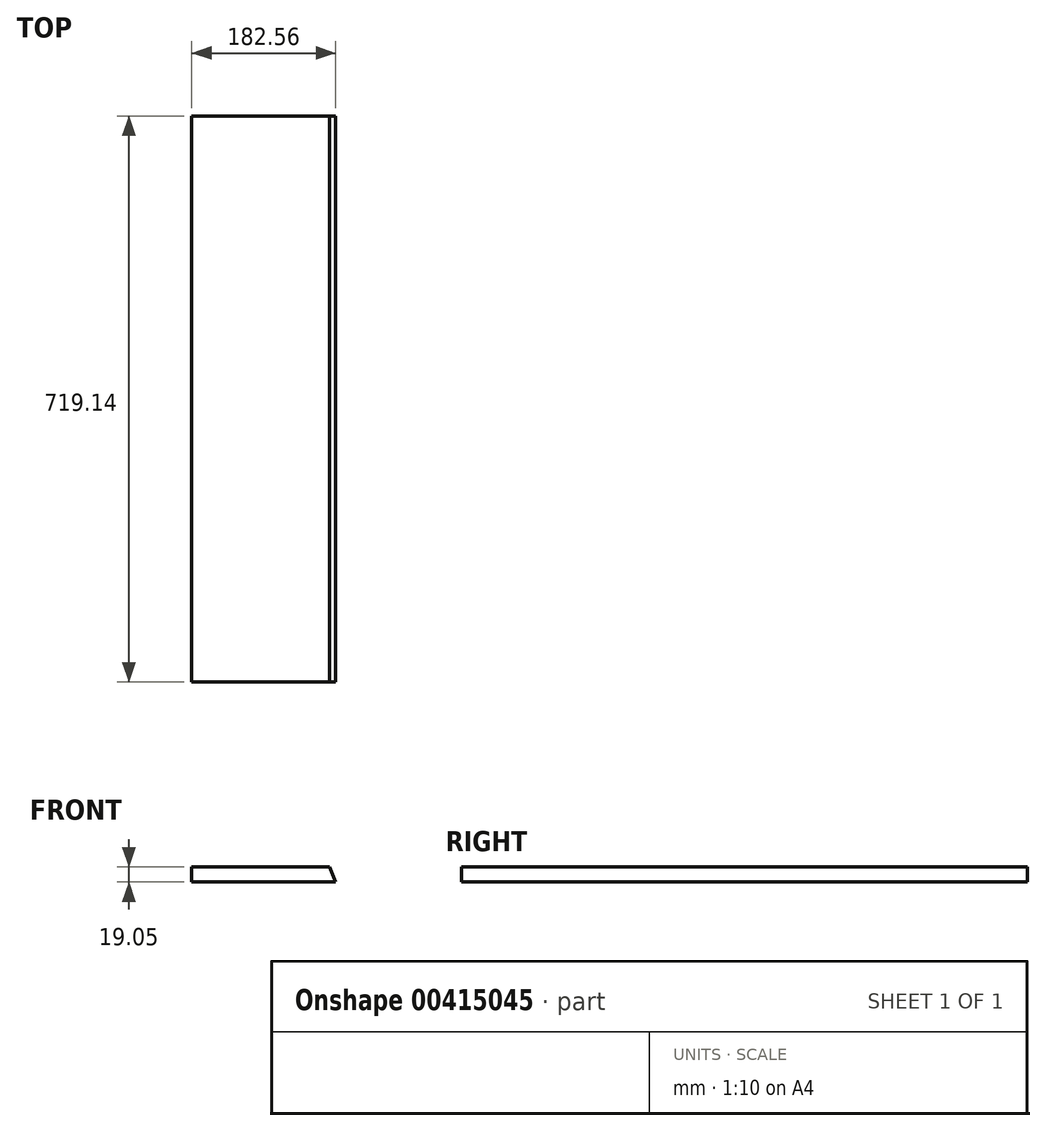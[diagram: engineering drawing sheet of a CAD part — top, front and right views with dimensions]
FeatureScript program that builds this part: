
annotation { "Feature Type Name" : "Feature", "Feature Type Description" : "" }
export const myFeature = defineFeature(function(context is Context, id is Id, definition is map)
    precondition{}
    {
        {
            var Q0;
            Q0=qCreatedBy(makeId("Front.planeOp"),FACE);
            var sketch = newSketch(context, id + "F0", { "sketchPlane" : qUnion([Q0])});
            skLineSegment(sketch, "E0.bottom", {"start": v(0, 0) * mm, "end": v(182.56, 0) * mm});
            skLineSegment(sketch, "E0.top", {"start": v(0, 19.05) * mm, "end": v(182.56, 19.05) * mm});
            skLineSegment(sketch, "E0.left", {"start": v(0, 0) * mm, "end": v(0, 19.05) * mm});
            skLineSegment(sketch, "E0.right", {"start": v(182.56, 0) * mm, "end": v(182.56, 19.05) * mm});
            skSolve(sketch);
        }
        {
            var Q0;
            Q0=makeQuery(id+"F0.imprint","IMPRINT",FACE,{"disambiguationData":[TD([[makeQuery(id+"F0.imprint","IMPRINT",EDGE,{"derivedFrom":sQuery(id+"F0.wireOp",EDGE,"E0.bottom")}),1.0]])]});
            extrude(context, id + "F1", {"entities" : qUnion([Q0]), "depth" : 719.14 * mm, "offsetDistance" : 25.4 * mm});
        }
        {
            var Q0;
            Q0=makeQuery(id+"F1.opExtrude","CAP_FACE",FACE,{"disambiguationData":[OSD([sQuery(id+"F0.wireOp",EDGE,"E0.bottom"),sQuery(id+"F0.wireOp",EDGE,"E0.top"),sQuery(id+"F0.wireOp",EDGE,"E0.left"),sQuery(id+"F0.wireOp",EDGE,"E0.right")])],"isStart":false});
            var sketch = newSketch(context, id + "F2", { "sketchPlane" : qUnion([Q0])});
            skLineSegment(sketch, "E1", {"start": v(182.56, 0) * mm, "end": v(174.67, 19.05) * mm});
            skSolve(sketch);
        }
        {
            var Q0;
            {var subQ0=sQuery(id+"F2.wireOp",EDGE,"E1");Q0=makeQuery(id+"F2.imprint","IMPRINT",FACE,{"disambiguationData":[TD([[makeQuery(id+"F2.imprint","IMPRINT",EDGE,{"derivedFrom":subQ0}),-1.0]])]});}
            extrude(context, id + "F3", {"entities" : qUnion([Q0]), "operationType" : NewBodyOperationType.REMOVE, "endBound" : BoundingType.THROUGH_ALL, "oppositeDirection" : true, "depth" : 25.4 * mm});
        }
    });
